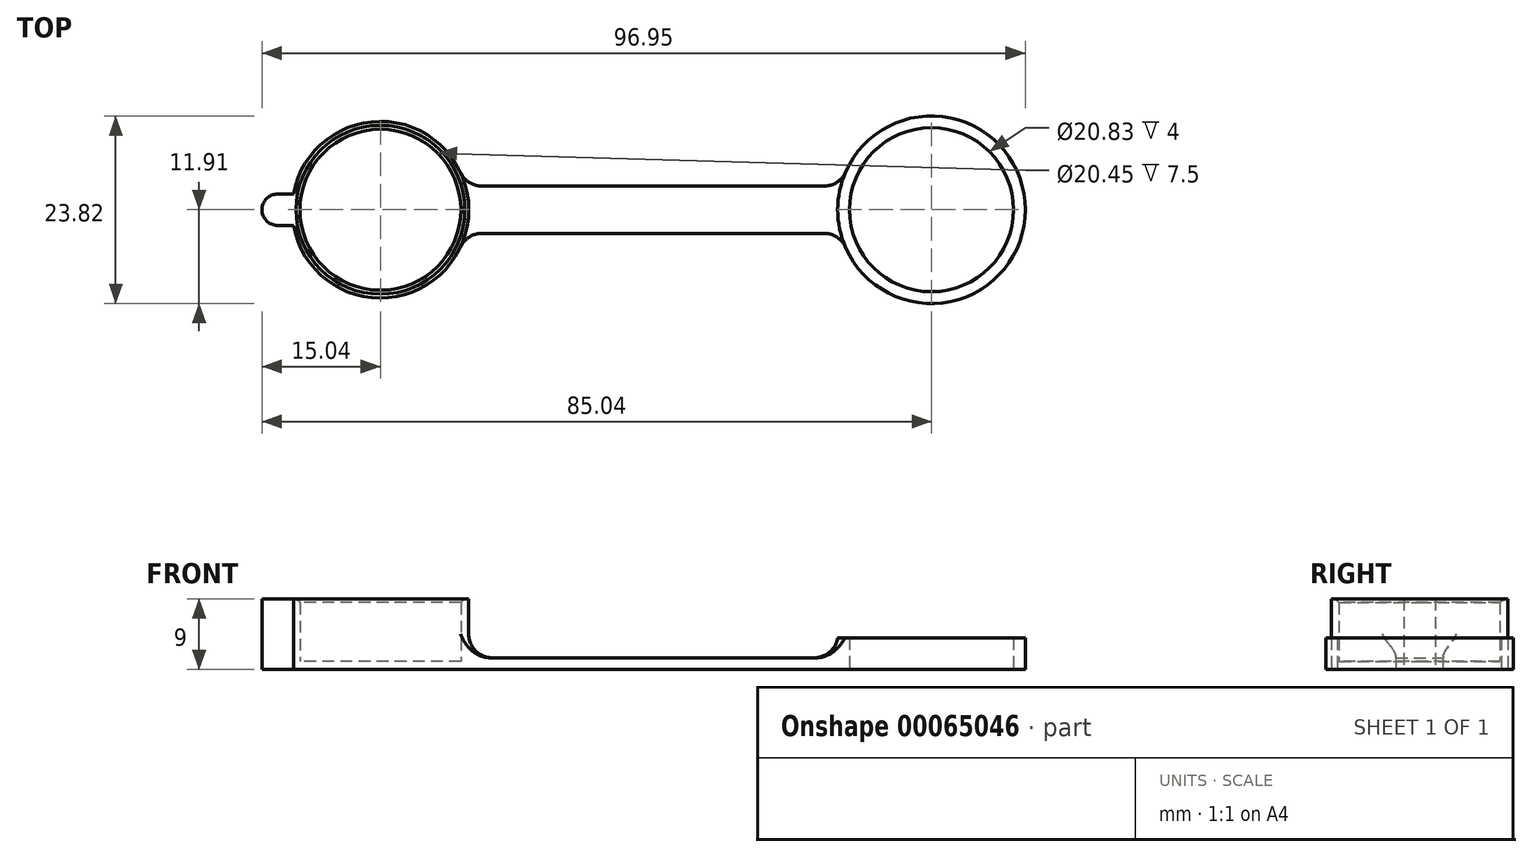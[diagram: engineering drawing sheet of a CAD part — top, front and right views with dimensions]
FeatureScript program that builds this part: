
annotation { "Feature Type Name" : "Feature", "Feature Type Description" : "" }
export const myFeature = defineFeature(function(context is Context, id is Id, definition is map)
    precondition{}
    {
        {
            var Q0;
            Q0=qCreatedBy(makeId("Top.planeOp"),FACE);
            var sketch = newSketch(context, id + "F0", { "sketchPlane" : qUnion([Q0])});
            skCircle(sketch, "E0", {"center": v(0, 0) * mm, "radius": 11.22 * mm});
            skLineSegment(sketch, "E1.bottom", {"start": v(-11.04, 2) * mm, "end": v(-15.04, 2) * mm});
            skLineSegment(sketch, "E1.top", {"start": v(-11.04, -2) * mm, "end": v(-15.04, -2) * mm});
            skLineSegment(sketch, "E1.left", {"start": v(-11.04, 2) * mm, "end": v(-11.04, -2) * mm, "construction": true});
            skLineSegment(sketch, "E1.right", {"start": v(-15.04, 2) * mm, "end": v(-15.04, -2) * mm});
            skSolve(sketch);
        }
        {
            var Q0;
            {var subQ0=sQuery(id+"F0.wireOp",EDGE,"E0");var subQ1=makeQuery(id+"F0.imprint","INTERSECT",VERTEX,{"derivedFrom":[subQ0,sQuery(id+"F0.wireOp",EDGE,"E1.bottom")]});Q0=makeQuery(id+"F0.imprint","IMPRINT",FACE,{"disambiguationData":[TD([[makeQuery(id+"F0.imprint","IMPRINT",EDGE,{"disambiguationData":[TD([[subQ1,-1.0]])],"derivedFrom":subQ0}),1.0]])]});}
            extrude(context, id + "F7", {"entities" : qUnion([Q0]), "depth" : (8 + 1) * mm});
        }
        {
            var Q0;
            Q0=qCreatedBy(makeId("Top.planeOp"),FACE);
            var sketch = newSketch(context, id + "F8", { "sketchPlane" : qUnion([Q0])});
            skLineSegment(sketch, "E2.bottom", {"start": v(70, 3) * mm, "end": v(58.47, 3) * mm, "construction": true});
            skLineSegment(sketch, "E2.top", {"start": v(70, -3) * mm, "end": v(58.47, -3) * mm, "construction": true});
            skLineSegment(sketch, "E2.left", {"start": v(70, 3) * mm, "end": v(70, -3) * mm});
            skLineSegment(sketch, "E2.right", {"start": v(0, 3) * mm, "end": v(0, -3) * mm});
            skCircle(sketch, "E3", {"center": v(70, 0) * mm, "radius": 10.41 * mm});
            skCircle(sketch, "E4", {"center": v(70, 0) * mm, "radius": 11.91 * mm});
            skLineSegment(sketch, "E5", {"start": v(70, 10.41) * mm, "end": v(70, 11.91) * mm});
            skLineSegment(sketch, "E6", {"start": v(58.47, 3) * mm, "end": v(0, 3) * mm});
            skLineSegment(sketch, "E7", {"start": v(58.47, -3) * mm, "end": v(0, -3) * mm});
            skSolve(sketch);
        }
        {
            var Q0;
            Q0 = qSketchRegion(id + "F8", true);
            extrude(context, id + "F9", {"entities" : qUnion([Q0]), "operationType" : NewBodyOperationType.ADD, "depth" : 1.5 * mm});
        }
        {
            var Q0;
            Q0=makeQuery(id+"F7.opExtrude","CAP_FACE",FACE,{"disambiguationData":[OSD([sQuery(id+"F0.wireOp",EDGE,"E0")])],"isStart":false});
            shell(context, id + "F1", {"entities" : qUnion([Q0]), "thickness" : 1 * mm});
        }
        {
            var Q0;
            {var subQ0=sQuery(id+"F0.wireOp",EDGE,"E1.bottom");Q0=makeQuery(id+"F0.imprint","IMPRINT",FACE,{"disambiguationData":[TD([[makeQuery(id+"F0.imprint","IMPRINT",EDGE,{"derivedFrom":subQ0}),1.0]])]});}
            var Q1;
            Q1=makeQuery(id+"F7.opExtrude","CAP_FACE",FACE,{"disambiguationData":[OSD([sQuery(id+"F0.wireOp",EDGE,"E0")])],"isStart":false});
            extrude(context, id + "F2", {"entities" : qUnion([Q0]), "operationType" : NewBodyOperationType.ADD, "endBound" : BoundingType.UP_TO_SURFACE, "endBoundEntityFace" : qUnion([Q1]), "depth" : 25 * mm});
        }
        {
            var Q0;
            {var subQ0=sQuery(id+"F0.wireOp",EDGE,"E0");Q0=makeQuery(id+"F1.opShell","OFFSET_EDGE",EDGE,{"disambiguationData":[OSD([subQ0]),TDD([makeQuery(id+"F7.opExtrude","CAP_EDGE",EDGE,{"disambiguationData":[OSD([subQ0])],"isStart":false})])]});}
            chamfer(context, id + "F3", {"entities" : qUnion([Q0]), "width" : 0.5 * mm});
        }
        {
            var Q0;
            Q0=makeQuery(id+"F8.imprint","IMPRINT",FACE,{"disambiguationData":[TD([[makeQuery(id+"F8.imprint","IMPRINT",EDGE,{"derivedFrom":sQuery(id+"F8.wireOp",EDGE,"E3")}),-1.0]])]});
            extrude(context, id + "F4", {"entities" : qUnion([Q0]), "operationType" : NewBodyOperationType.ADD, "depth" : 4 * mm});
        }
        {
            var Q0;
            Q0=makeQuery(id+"F2.opExtrude","SWEPT_EDGE",EDGE,{"disambiguationData":[OSD([sQuery(id+"F0.wireOp",EDGE,"E0"),sQuery(id+"F0.wireOp",EDGE,"E1.bottom")])]});
            var Q1;
            Q1=makeQuery(id+"F2.opExtrude","SWEPT_EDGE",EDGE,{"disambiguationData":[OSD([sQuery(id+"F0.wireOp",EDGE,"E0"),sQuery(id+"F0.wireOp",EDGE,"E1.top")])]});
            var Q2;
            Q2=makeQuery(id+"F2.opExtrude","SWEPT_EDGE",EDGE,{"disambiguationData":[OSD([sQuery(id+"F0.wireOp",EDGE,"E1.top"),sQuery(id+"F0.wireOp",EDGE,"E1.right")])]});
            var Q3;
            Q3=makeQuery(id+"F2.opExtrude","SWEPT_EDGE",EDGE,{"disambiguationData":[OSD([sQuery(id+"F0.wireOp",EDGE,"E1.bottom"),sQuery(id+"F0.wireOp",EDGE,"E1.right")])]});
            fillet(context, id + "F5", {"entities" : qUnion([Q0, Q1, Q2, Q3]), "radius" : 2 * mm, "allowEdgeOverflow" : false});
        }
        {
            var Q0;
            Q0=makeQuery(id+"F9.opExtrude","SWEPT_EDGE",EDGE,{"disambiguationData":[OSD([sQuery(id+"F8.wireOp",EDGE,"E4"),sQuery(id+"F8.wireOp",EDGE,"E7")])]});
            var Q1;
            Q1=makeQuery(id+"F9.opExtrude","SWEPT_EDGE",EDGE,{"disambiguationData":[OSD([sQuery(id+"F8.wireOp",EDGE,"E4"),sQuery(id+"F8.wireOp",EDGE,"E6")])]});
            var Q2;
            {var subQ0=sQuery(id+"F8.wireOp",EDGE,"E4");Q2=makeQuery(id+"F4.boolean.opBoolean","INTERSECT",EDGE,{"derivedFrom":[makeQuery(id+"F9.opExtrude","CAP_FACE",FACE,{"disambiguationData":[OSD([sQuery(id+"F8.wireOp",EDGE,"E2.right"),sQuery(id+"F8.wireOp",EDGE,"E3"),subQ0,sQuery(id+"F8.wireOp",EDGE,"E6"),sQuery(id+"F8.wireOp",EDGE,"E7")])],"isStart":false}),makeQuery(id+"F4.opExtrude","SWEPT_FACE",FACE,{"disambiguationData":[OSD([subQ0])]})]});}
            var Q3;
            Q3=makeQuery(id+"F9.boolean.opBoolean","INTERSECT",EDGE,{"derivedFrom":[makeQuery(id+"F7.opExtrude","SWEPT_FACE",FACE,{"disambiguationData":[OSD([sQuery(id+"F0.wireOp",EDGE,"E0")])]}),makeQuery(id+"F9.opExtrude","CAP_FACE",FACE,{"disambiguationData":[OSD([sQuery(id+"F8.wireOp",EDGE,"E2.right"),sQuery(id+"F8.wireOp",EDGE,"E3"),sQuery(id+"F8.wireOp",EDGE,"E4"),sQuery(id+"F8.wireOp",EDGE,"E6"),sQuery(id+"F8.wireOp",EDGE,"E7")])],"isStart":false})]});
            var Q4;
            Q4=makeQuery(id+"F9.boolean.opBoolean","INTERSECT",EDGE,{"derivedFrom":[makeQuery(id+"F7.opExtrude","SWEPT_FACE",FACE,{"disambiguationData":[OSD([sQuery(id+"F0.wireOp",EDGE,"E0")])]}),makeQuery(id+"F9.opExtrude","SWEPT_FACE",FACE,{"disambiguationData":[OSD([sQuery(id+"F8.wireOp",EDGE,"E7")])]})]});
            var Q5;
            Q5=makeQuery(id+"F9.boolean.opBoolean","INTERSECT",EDGE,{"derivedFrom":[makeQuery(id+"F7.opExtrude","SWEPT_FACE",FACE,{"disambiguationData":[OSD([sQuery(id+"F0.wireOp",EDGE,"E0")])]}),makeQuery(id+"F9.opExtrude","SWEPT_FACE",FACE,{"disambiguationData":[OSD([sQuery(id+"F8.wireOp",EDGE,"E6")])]})]});
            fillet(context, id + "F6", {"entities" : qUnion([Q0, Q1, Q2, Q3, Q4, Q5]), "radius" : 3 * mm, "allowEdgeOverflow" : false});
        }
    });
